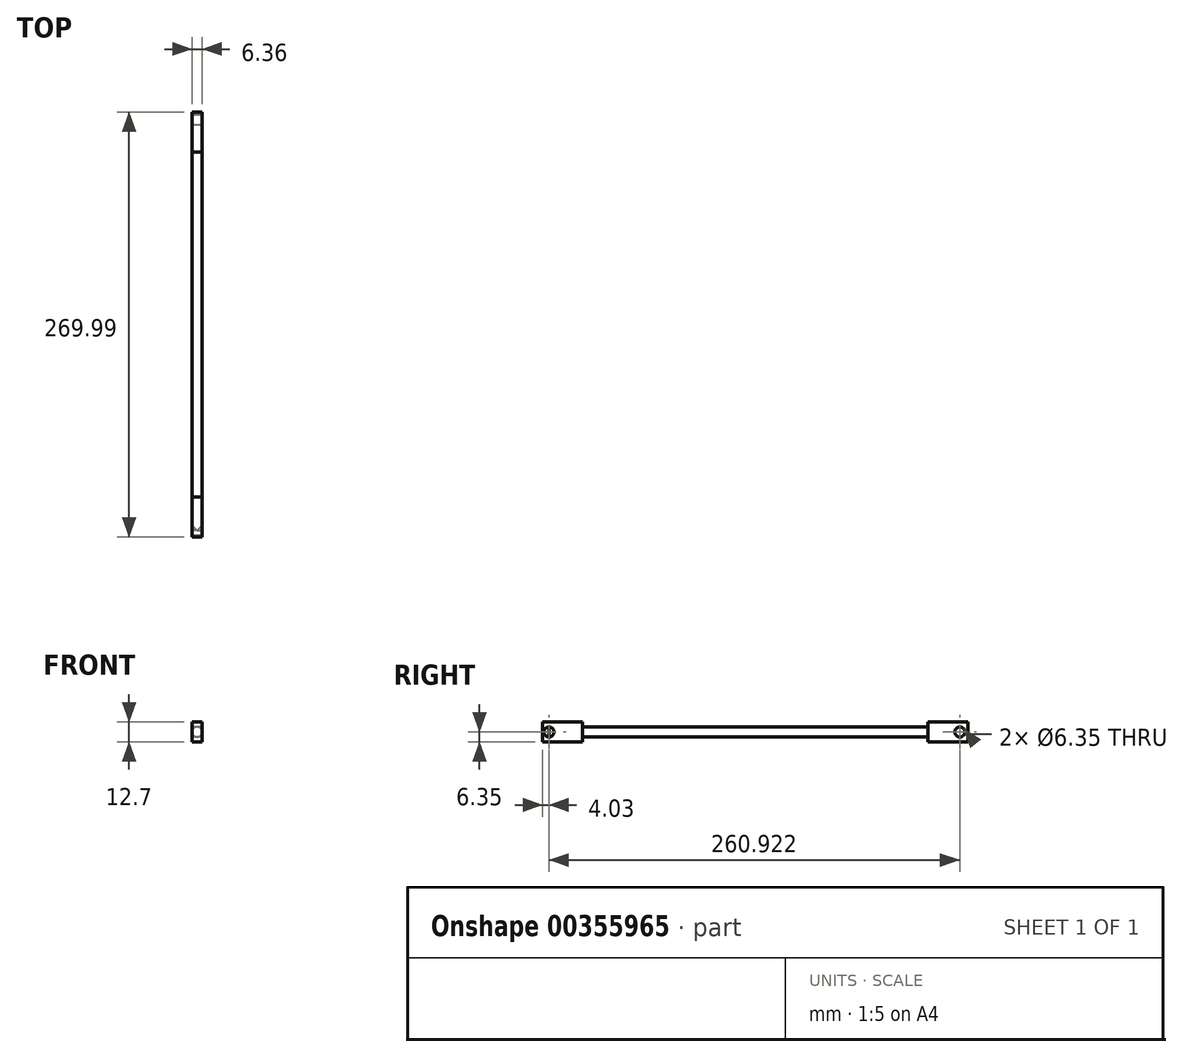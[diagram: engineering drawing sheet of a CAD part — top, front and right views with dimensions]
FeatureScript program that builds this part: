
annotation { "Feature Type Name" : "Feature", "Feature Type Description" : "" }
export const myFeature = defineFeature(function(context is Context, id is Id, definition is map)
    precondition{}
    {
        {
            var Q0;
            Q0=qCreatedBy(makeId("Right.planeOp"),FACE);
            var sketch = newSketch(context, id + "F0", { "sketchPlane" : qUnion([Q0])});
            skCircle(sketch, "E0", {"center": v(0, 0) * mm, "radius": 3.18 * mm});
            skLineSegment(sketch, "E1.bottom", {"start": v(21.37, -6.35) * mm, "end": v(-4.03, -6.35) * mm});
            skLineSegment(sketch, "E1.top", {"start": v(21.37, 6.35) * mm, "end": v(-4.03, 6.35) * mm});
            skLineSegment(sketch, "E1.left", {"start": v(21.37, -6.35) * mm, "end": v(21.37, 6.35) * mm});
            skLineSegment(sketch, "E1.right", {"start": v(-4.03, -6.35) * mm, "end": v(-4.03, 6.35) * mm});
            skPoint(sketch, "E1.middle", {"position": v(8.67, 0) * mm});
            skSolve(sketch);
        }
        {
            var Q0;
            Q0=qCreatedBy(makeId("Front.planeOp"),FACE);
            var sketch = newSketch(context, id + "F1", { "sketchPlane" : qUnion([Q0])});
            skCircle(sketch, "E2", {"center": v(0, 0) * mm, "radius": 3.18 * mm});
            skSolve(sketch);
        }
        {
            var Q0;
            Q0=makeQuery(id+"F1.imprint","IMPRINT",FACE,{"disambiguationData":[TD([[makeQuery(id+"F1.imprint","IMPRINT",EDGE,{"derivedFrom":sQuery(id+"F1.wireOp",EDGE,"E2")}),1.0]])]});
            extrude(context, id + "F2", {"entities" : qUnion([Q0]), "oppositeDirection" : true, "depth" : 254 * mm});
        }
        {
            var Q0;
            Q0=makeQuery(id+"F0.imprint","IMPRINT",FACE,{"disambiguationData":[TD([[makeQuery(id+"F0.imprint","IMPRINT",EDGE,{"derivedFrom":sQuery(id+"F0.wireOp",EDGE,"E0")}),-1.0]])]});
            extrude(context, id + "F3", {"entities" : qUnion([Q0]), "operationType" : NewBodyOperationType.ADD, "endBound" : BoundingType.SYMMETRIC, "depth" : 6.35 * mm});
        }
        {
            var Q0;
            Q0=qCreatedBy(makeId("Right.planeOp"),FACE);
            var sketch = newSketch(context, id + "F4", { "sketchPlane" : qUnion([Q0])});
            skLineSegment(sketch, "E3.bottom", {"start": v(265.96, -6.35) * mm, "end": v(240.56, -6.35) * mm});
            skLineSegment(sketch, "E3.top", {"start": v(265.96, 6.35) * mm, "end": v(240.56, 6.35) * mm});
            skLineSegment(sketch, "E3.left", {"start": v(265.96, -6.35) * mm, "end": v(265.96, 6.35) * mm});
            skLineSegment(sketch, "E3.right", {"start": v(240.56, -6.35) * mm, "end": v(240.56, 6.35) * mm});
            skPoint(sketch, "E3.middle", {"position": v(253.26, 0) * mm});
            skCircle(sketch, "E4", {"center": v(260.92, 0) * mm, "radius": 3.18 * mm});
            skSolve(sketch);
        }
        {
            var Q0;
            Q0=makeQuery(id+"F4.imprint","IMPRINT",FACE,{"disambiguationData":[TD([[makeQuery(id+"F4.imprint","IMPRINT",EDGE,{"derivedFrom":sQuery(id+"F4.wireOp",EDGE,"E3.bottom")}),-1.0]])]});
            extrude(context, id + "F5", {"entities" : qUnion([Q0]), "operationType" : NewBodyOperationType.ADD, "endBound" : BoundingType.SYMMETRIC, "depth" : 6.35 * mm});
        }
    });
